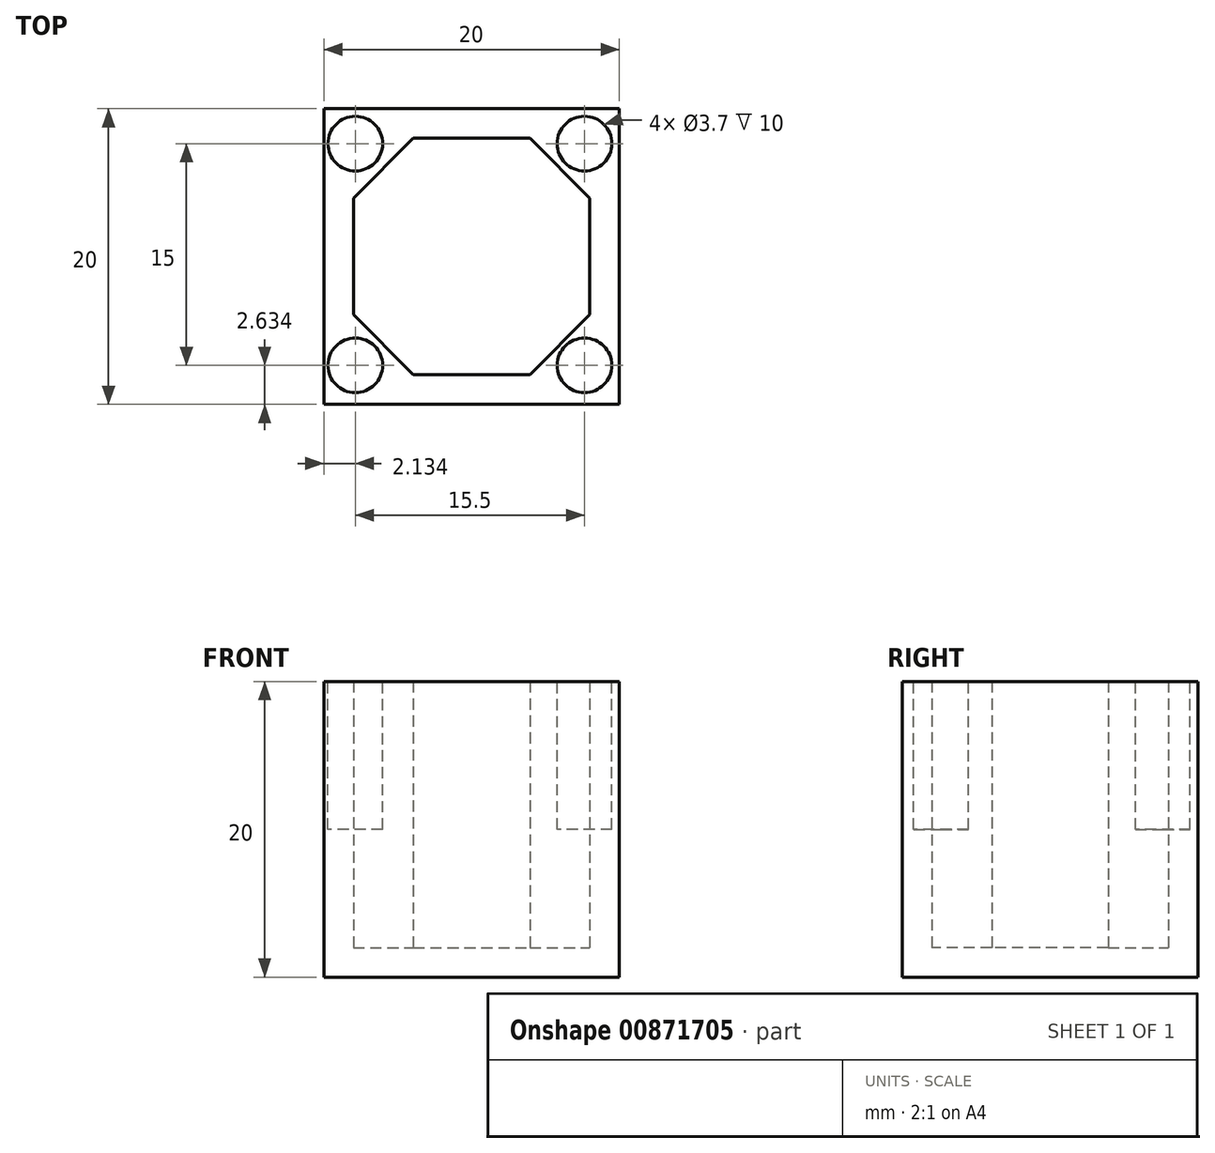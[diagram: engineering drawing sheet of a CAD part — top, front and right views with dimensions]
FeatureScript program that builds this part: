
annotation { "Feature Type Name" : "Feature", "Feature Type Description" : "" }
export const myFeature = defineFeature(function(context is Context, id is Id, definition is map)
    precondition{}
    {
        {
            assignVariable(context, id + "F0", {"name" : "height", "anyValue" : 20});
        }
        {
            assignVariable(context, id + "F1", {"name" : "wall_width", "anyValue" : 2});
        }
        {
            var Q0;
            Q0=qCreatedBy(makeId("Top.planeOp"),FACE);
            var sketch = newSketch(context, id + "F2", { "sketchPlane" : qUnion([Q0])});
            skLineSegment(sketch, "E0.bottom", {"start": v(0, 0) * mm, "end": v(20, 0) * mm});
            skLineSegment(sketch, "E0.top", {"start": v(0, -20) * mm, "end": v(20, -20) * mm});
            skLineSegment(sketch, "E0.left", {"start": v(0, 0) * mm, "end": v(0, -20) * mm});
            skLineSegment(sketch, "E0.right", {"start": v(20, 0) * mm, "end": v(20, -20) * mm});
            skSolve(sketch);
        }
        {
            var Q0;
            Q0 = qSketchRegion(id + "F2", true);
            extrude(context, id + "F3", {"entities" : qUnion([Q0]), "depth" : (getVariable(context, 'wall_width')) * mm, "offsetDistance" : 25 * mm});
        }
        {
            var Q0;
            Q0=makeQuery(id+"F3.opExtrude","CAP_FACE",FACE,{"disambiguationData":[OSD([sQuery(id+"F2.wireOp",EDGE,"E0.bottom"),sQuery(id+"F2.wireOp",EDGE,"E0.top"),sQuery(id+"F2.wireOp",EDGE,"E0.left"),sQuery(id+"F2.wireOp",EDGE,"E0.right")])],"isStart":false});
            var sketch = newSketch(context, id + "F4", { "sketchPlane" : qUnion([Q0])});
            skLineSegment(sketch, "E1.bottom", {"start": v(2, -2) * mm, "end": v(18, -2) * mm});
            skLineSegment(sketch, "E1.top", {"start": v(2, -18) * mm, "end": v(18, -18) * mm});
            skLineSegment(sketch, "E1.left", {"start": v(2, -2) * mm, "end": v(2, -18) * mm});
            skLineSegment(sketch, "E1.right", {"start": v(18, -2) * mm, "end": v(18, -18) * mm});
            skLineSegment(sketch, "E2", {"start": v(2, -2) * mm, "end": v(2, 0) * mm, "construction": true});
            skLineSegment(sketch, "E3", {"start": v(2, -18) * mm, "end": v(0, -18) * mm, "construction": true});
            skLineSegment(sketch, "E4", {"start": v(18, -18) * mm, "end": v(18, -20) * mm, "construction": true});
            skLineSegment(sketch, "E5", {"start": v(18, -2) * mm, "end": v(20, -2) * mm, "construction": true});
            skLineSegment(sketch, "E6", {"start": v(2, -6.06) * mm, "end": v(6.06, -2) * mm});
            skLineSegment(sketch, "E7", {"start": v(2, -13.94) * mm, "end": v(6.06, -18) * mm});
            skLineSegment(sketch, "E8", {"start": v(13.94, -18) * mm, "end": v(18, -13.94) * mm});
            skLineSegment(sketch, "E9", {"start": v(13.94, -2) * mm, "end": v(18, -6.06) * mm});
            skSolve(sketch);
        }
        {
            var Q0;
            Q0=makeQuery(id+"F4.imprint","IMPRINT",FACE,{"disambiguationData":[TD([[makeQuery(id+"F4.imprint","IMPRINT",EDGE,{"derivedFrom":sQuery(id+"F4.wireOp",EDGE,"E1.bottom")}),1.0]])]});
            var Q1;
            {var subQ3=sQuery(id+"F4.wireOp",EDGE,"E6");Q1=makeQuery(id+"F4.imprint","IMPRINT",FACE,{"disambiguationData":[TD([[makeQuery(id+"F4.imprint","IMPRINT",EDGE,{"derivedFrom":subQ3}),1.0]])]});}
            var Q2;
            {var subQ3=sQuery(id+"F4.wireOp",EDGE,"E9");Q2=makeQuery(id+"F4.imprint","IMPRINT",FACE,{"disambiguationData":[TD([[makeQuery(id+"F4.imprint","IMPRINT",EDGE,{"derivedFrom":subQ3}),1.0]])]});}
            var Q3;
            {var subQ3=sQuery(id+"F4.wireOp",EDGE,"E8");Q3=makeQuery(id+"F4.imprint","IMPRINT",FACE,{"disambiguationData":[TD([[makeQuery(id+"F4.imprint","IMPRINT",EDGE,{"derivedFrom":subQ3}),-1.0]])]});}
            var Q4;
            {var subQ3=sQuery(id+"F4.wireOp",EDGE,"E7");Q4=makeQuery(id+"F4.imprint","IMPRINT",FACE,{"disambiguationData":[TD([[makeQuery(id+"F4.imprint","IMPRINT",EDGE,{"derivedFrom":subQ3}),-1.0]])]});}
            extrude(context, id + "F5", {"entities" : qUnion([Q0, Q1, Q2, Q3, Q4]), "operationType" : NewBodyOperationType.ADD, "depth" : (getVariable(context, 'height') - getVariable(context, 'wall_width')) * mm, "offsetDistance" : 25 * mm});
        }
        {
            var Q0;
            Q0=makeQuery(id+"F5.opExtrude","CAP_FACE",FACE,{"disambiguationData":[OSD([sQuery(id+"F2.wireOp",EDGE,"E0.bottom"),sQuery(id+"F2.wireOp",EDGE,"E0.top"),sQuery(id+"F2.wireOp",EDGE,"E0.left"),sQuery(id+"F2.wireOp",EDGE,"E0.right"),sQuery(id+"F4.wireOp",EDGE,"E1.bottom"),sQuery(id+"F4.wireOp",EDGE,"E1.top"),sQuery(id+"F4.wireOp",EDGE,"E1.left"),sQuery(id+"F4.wireOp",EDGE,"E1.right")])],"isStart":false});
            var sketch = newSketch(context, id + "F6", { "sketchPlane" : qUnion([Q0])});
            skCircle(sketch, "E10", {"center": v(2.13, -2.37) * mm, "radius": 1.85 * mm});
            skCircle(sketch, "E11", {"center": v(17.63, -2.37) * mm, "radius": 1.85 * mm});
            skCircle(sketch, "E12", {"center": v(17.63, -17.37) * mm, "radius": 1.85 * mm});
            skCircle(sketch, "E13", {"center": v(2.13, -17.37) * mm, "radius": 1.85 * mm});
            skLineSegment(sketch, "E14", {"start": v(2.13, -17.37) * mm, "end": v(4.03, -15.97) * mm, "construction": true});
            skLineSegment(sketch, "E15", {"start": v(15.97, -4.03) * mm, "end": v(17.63, -2.37) * mm, "construction": true});
            skSolve(sketch);
        }
        {
            var Q0;
            Q0=makeQuery(id+"F6.imprint","IMPRINT",FACE,{"disambiguationData":[TD([[makeQuery(id+"F6.imprint","IMPRINT",EDGE,{"derivedFrom":sQuery(id+"F6.wireOp",EDGE,"E10")}),1.0]])]});
            var Q1;
            Q1=makeQuery(id+"F6.imprint","IMPRINT",FACE,{"disambiguationData":[TD([[makeQuery(id+"F6.imprint","IMPRINT",EDGE,{"derivedFrom":sQuery(id+"F6.wireOp",EDGE,"E11")}),1.0]])]});
            var Q2;
            Q2=makeQuery(id+"F6.imprint","IMPRINT",FACE,{"disambiguationData":[TD([[makeQuery(id+"F6.imprint","IMPRINT",EDGE,{"derivedFrom":sQuery(id+"F6.wireOp",EDGE,"E12")}),1.0]])]});
            var Q3;
            Q3=makeQuery(id+"F6.imprint","IMPRINT",FACE,{"disambiguationData":[TD([[makeQuery(id+"F6.imprint","IMPRINT",EDGE,{"derivedFrom":sQuery(id+"F6.wireOp",EDGE,"E13")}),1.0]])]});
            extrude(context, id + "F7", {"entities" : qUnion([Q0, Q1, Q2, Q3]), "operationType" : NewBodyOperationType.REMOVE, "oppositeDirection" : true, "depth" : 10 * mm, "offsetDistance" : 25 * mm});
        }
    });
